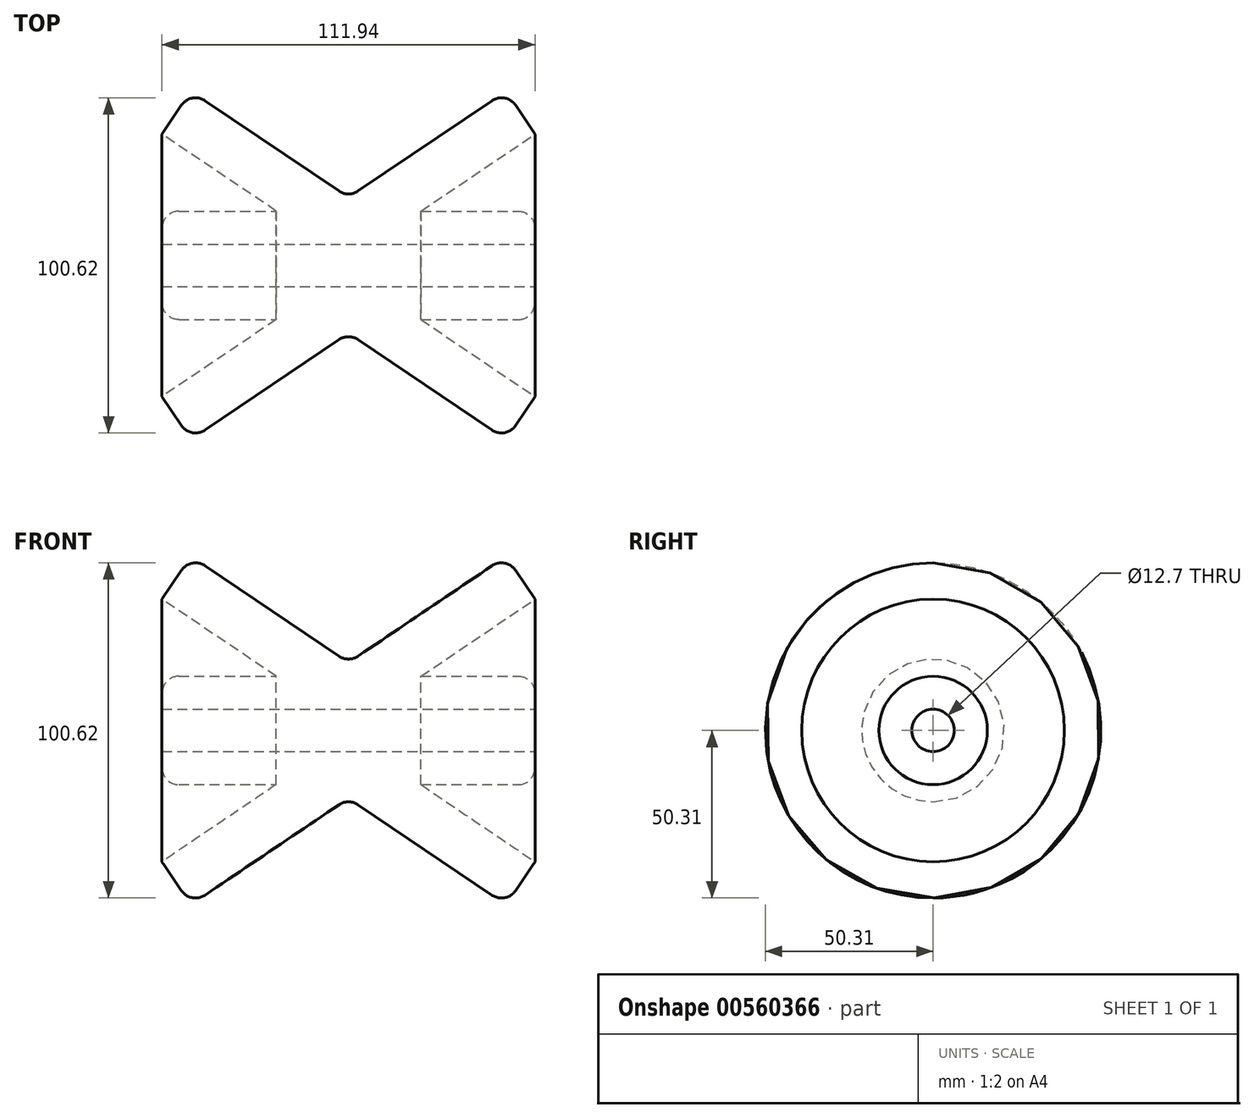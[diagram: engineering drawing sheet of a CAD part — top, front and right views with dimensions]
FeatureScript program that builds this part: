
annotation { "Feature Type Name" : "Feature", "Feature Type Description" : "" }
export const myFeature = defineFeature(function(context is Context, id is Id, definition is map)
    precondition{}
    {
        {
            var Q0;
            Q0=qCreatedBy(makeId("Front.planeOp"),FACE);
            var sketch = newSketch(context, id + "F0", { "sketchPlane" : qUnion([Q0])});
            skLineSegment(sketch, "E0", {"start": v(0, 0) * mm, "end": v(-55.97, 0) * mm});
            skLineSegment(sketch, "E1", {"start": v(-55.97, 0) * mm, "end": v(-55.97, 16.28) * mm});
            skLineSegment(sketch, "E2", {"start": v(-55.97, 16.28) * mm, "end": v(-21.7, 16.28) * mm});
            skLineSegment(sketch, "E3", {"start": v(-21.7, 16.28) * mm, "end": v(-55.97, 39.4) * mm});
            skLineSegment(sketch, "E4", {"start": v(-55.97, 39.4) * mm, "end": v(-47.28, 52.28) * mm});
            skLineSegment(sketch, "E5", {"start": v(-47.28, 52.28) * mm, "end": v(0, 20.37) * mm});
            skLineSegment(sketch, "E6", {"start": v(0, 0) * mm, "end": v(55.97, 0) * mm});
            skLineSegment(sketch, "E7", {"start": v(55.97, 0) * mm, "end": v(55.97, 16.28) * mm});
            skLineSegment(sketch, "E8", {"start": v(55.97, 16.28) * mm, "end": v(21.7, 16.28) * mm});
            skLineSegment(sketch, "E9", {"start": v(21.7, 16.28) * mm, "end": v(55.97, 39.4) * mm});
            skLineSegment(sketch, "E10", {"start": v(55.97, 39.4) * mm, "end": v(47.28, 52.28) * mm});
            skLineSegment(sketch, "E11", {"start": v(47.28, 52.28) * mm, "end": v(0, 20.37) * mm});
            skSolve(sketch);
        }
        {
            var Q0;
            Q0=makeQuery(id+"F0.imprint","IMPRINT",FACE,{"disambiguationData":[TD([[makeQuery(id+"F0.imprint","IMPRINT",EDGE,{"derivedFrom":sQuery(id+"F0.wireOp",EDGE,"E0")}),-1.0]])]});
            var Q1;
            Q1=sQuery(id+"F0.wireOp",EDGE,"E6");
            revolve(context, id + "F1", {"entities" : qUnion([Q0]), "axis" : qUnion([Q1]), "revolveType" : RevolveType.ONE_DIRECTION, "oppositeDirection" : true, "angle" : 360 * degree});
        }
        {
            var Q0;
            Q0=makeQuery(id+"F1.opRevolve","SWEPT_FACE",FACE,{"disambiguationData":[OSD([sQuery(id+"F0.wireOp",EDGE,"E1")])]});
            fillet(context, id + "F2", {"entities" : qUnion([Q0]), "radius" : 5.08 * mm, "tangentPropagation" : true, "allowEdgeOverflow" : false});
        }
        {
            var Q0;
            Q0=makeQuery(id+"F1.opRevolve","SWEPT_FACE",FACE,{"disambiguationData":[OSD([sQuery(id+"F0.wireOp",EDGE,"E7")])]});
            fillet(context, id + "F3", {"entities" : qUnion([Q0]), "radius" : 5.08 * mm, "tangentPropagation" : true, "allowEdgeOverflow" : false});
        }
        {
            var Q0;
            Q0=makeQuery(id+"F1.opRevolve","SWEPT_EDGE",EDGE,{"disambiguationData":[OSD([sQuery(id+"F0.wireOp",EDGE,"E4"),sQuery(id+"F0.wireOp",EDGE,"E5")])]});
            var Q1;
            Q1=makeQuery(id+"F1.opRevolve","SWEPT_EDGE",EDGE,{"disambiguationData":[OSD([sQuery(id+"F0.wireOp",EDGE,"E10"),sQuery(id+"F0.wireOp",EDGE,"E11")])]});
            fillet(context, id + "F4", {"entities" : qUnion([Q0, Q1]), "radius" : 5.08 * mm, "tangentPropagation" : true, "allowEdgeOverflow" : false});
        }
        {
            var Q0;
            Q0=makeQuery(id+"F1.opRevolve","SWEPT_EDGE",EDGE,{"disambiguationData":[OSD([sQuery(id+"F0.wireOp",EDGE,"E5"),sQuery(id+"F0.wireOp",EDGE,"E11")])]});
            fillet(context, id + "F5", {"entities" : qUnion([Q0]), "radius" : 5.08 * mm, "tangentPropagation" : true, "allowEdgeOverflow" : false});
        }
        {
            var Q0;
            Q0=makeQuery(id+"F1.opRevolve","SWEPT_FACE",FACE,{"disambiguationData":[OSD([sQuery(id+"F0.wireOp",EDGE,"E7")])]});
            var sketch = newSketch(context, id + "F6", { "sketchPlane" : qUnion([Q0])});
            skCircle(sketch, "E12", {"center": v(0, 0) * mm, "radius": 6.35 * mm});
            skSolve(sketch);
        }
        {
            var Q0;
            Q0=makeQuery(id+"F6.imprint","IMPRINT",FACE,{"disambiguationData":[TD([[makeQuery(id+"F6.imprint","IMPRINT",EDGE,{"derivedFrom":sQuery(id+"F6.wireOp",EDGE,"E12")}),1.0]])]});
            extrude(context, id + "F7", {"entities" : qUnion([Q0]), "operationType" : NewBodyOperationType.REMOVE, "endBound" : BoundingType.THROUGH_ALL, "oppositeDirection" : true, "depth" : 25.4 * mm, "offsetDistance" : 25.4 * mm});
        }
    });
